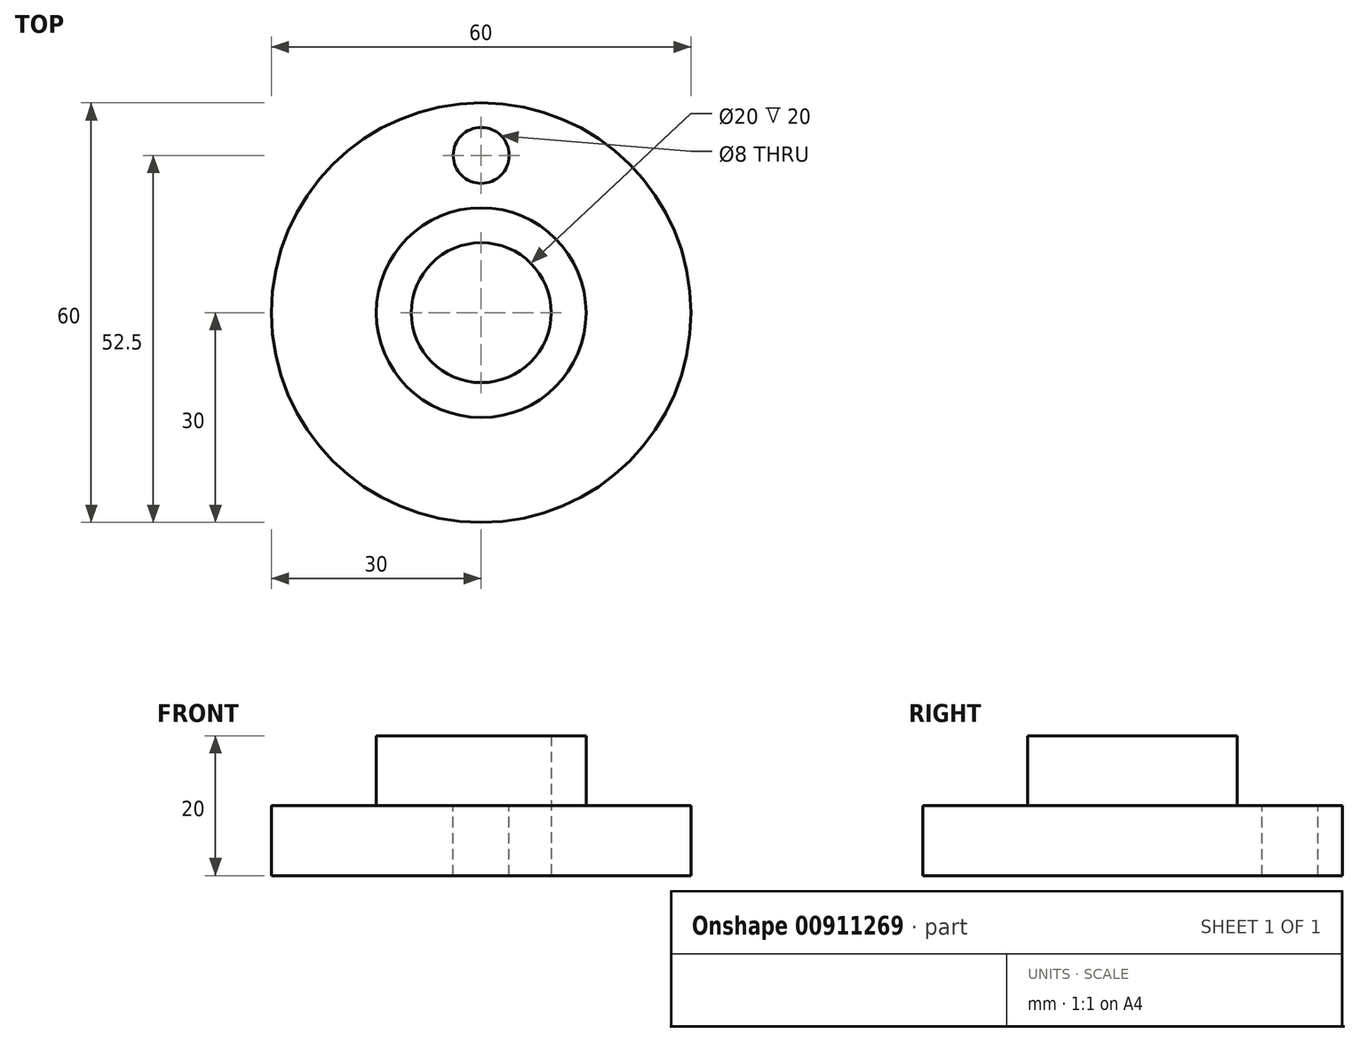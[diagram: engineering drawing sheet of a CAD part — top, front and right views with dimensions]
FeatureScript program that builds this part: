
annotation { "Feature Type Name" : "Feature", "Feature Type Description" : "" }
export const myFeature = defineFeature(function(context is Context, id is Id, definition is map)
    precondition{}
    {
        {
            var Q0;
            Q0=qCreatedBy(makeId("Top.planeOp"),FACE);
            var sketch = newSketch(context, id + "F0", { "sketchPlane" : qUnion([Q0])});
            skCircle(sketch, "E0", {"center": v(0, 0) * mm, "radius": 30 * mm});
            skCircle(sketch, "E1", {"center": v(0, 0) * mm, "radius": 10 * mm});
            skSolve(sketch);
        }
        {
            var Q0;
            Q0=makeQuery(id+"F0.imprint","IMPRINT",FACE,{"disambiguationData":[TD([[makeQuery(id+"F0.imprint","IMPRINT",EDGE,{"derivedFrom":sQuery(id+"F0.wireOp",EDGE,"E0")}),1.0]])]});
            extrude(context, id + "F1", {"entities" : qUnion([Q0]), "depth" : 10 * mm, "offsetDistance" : 25 * mm});
        }
        {
            var Q0;
            Q0=makeQuery(id+"F1.opExtrude","CAP_FACE",FACE,{"disambiguationData":[OSD([sQuery(id+"F0.wireOp",EDGE,"E0"),sQuery(id+"F0.wireOp",EDGE,"E1")])],"isStart":false});
            var sketch = newSketch(context, id + "F2", { "sketchPlane" : qUnion([Q0])});
            skCircle(sketch, "E2", {"center": v(0, 0) * mm, "radius": 10 * mm});
            skCircle(sketch, "E3", {"center": v(0, 0) * mm, "radius": 15 * mm});
            skSolve(sketch);
        }
        {
            var Q0;
            Q0 = qSketchRegion(id + "F2", true);
            extrude(context, id + "F3", {"entities" : qUnion([Q0]), "operationType" : NewBodyOperationType.ADD, "depth" : 10 * mm, "offsetDistance" : 25 * mm});
        }
        {
            var Q0;
            Q0=makeQuery(id+"F1.opExtrude","CAP_FACE",FACE,{"disambiguationData":[OSD([sQuery(id+"F0.wireOp",EDGE,"E0"),sQuery(id+"F0.wireOp",EDGE,"E1")])],"isStart":false});
            var sketch = newSketch(context, id + "F4", { "sketchPlane" : qUnion([Q0])});
            skCircle(sketch, "E4", {"center": v(0, 22.5) * mm, "radius": 4 * mm});
            skSolve(sketch);
        }
        {
            var Q0;
            Q0=makeQuery(id+"F4.imprint","IMPRINT",FACE,{"disambiguationData":[TD([[makeQuery(id+"F4.imprint","IMPRINT",EDGE,{"derivedFrom":sQuery(id+"F4.wireOp",EDGE,"E4")}),1.0]])]});
            extrude(context, id + "F5", {"entities" : qUnion([Q0]), "operationType" : NewBodyOperationType.REMOVE, "endBound" : BoundingType.THROUGH_ALL, "oppositeDirection" : true, "depth" : 25 * mm, "offsetDistance" : 25 * mm});
        }
    });
